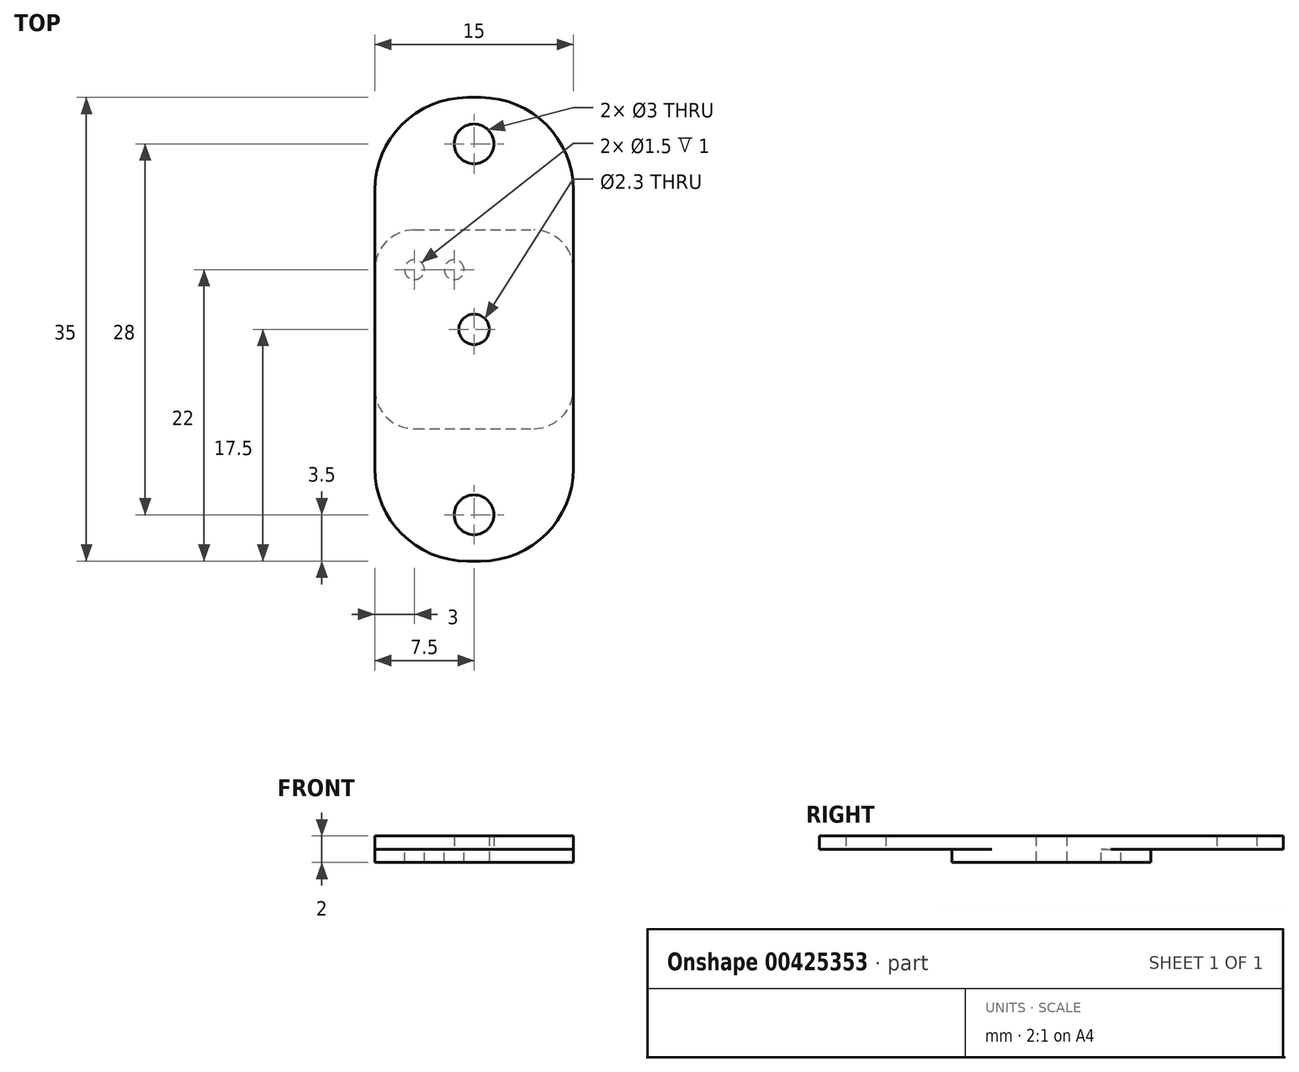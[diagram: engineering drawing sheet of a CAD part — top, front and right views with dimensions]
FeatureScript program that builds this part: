
annotation { "Feature Type Name" : "Feature", "Feature Type Description" : "" }
export const myFeature = defineFeature(function(context is Context, id is Id, definition is map)
    precondition{}
    {
        {
            var Q0;
            Q0=qCreatedBy(makeId("Top.planeOp"),FACE);
            var sketch = newSketch(context, id + "F0", { "sketchPlane" : qUnion([Q0])});
            skCircle(sketch, "E0", {"center": v(0, 0) * mm, "radius": 1.15 * mm});
            skCircle(sketch, "E1", {"center": v(0, 0) * mm, "radius": 2.5 * mm});
            skSolve(sketch);
        }
        {
            var Q0;
            Q0=makeQuery(id+"F0.imprint","IMPRINT",FACE,{"disambiguationData":[TD([[makeQuery(id+"F0.imprint","IMPRINT",EDGE,{"derivedFrom":sQuery(id+"F0.wireOp",EDGE,"E0")}),-1.0]])]});
            extrude(context, id + "F1", {"entities" : qUnion([Q0]), "depth" : 1 * mm});
        }
        {
            var Q0;
            Q0=makeQuery(id+"F1.opExtrude","CAP_FACE",FACE,{"disambiguationData":[OSD([sQuery(id+"F0.wireOp",EDGE,"E0"),sQuery(id+"F0.wireOp",EDGE,"E1")])],"isStart":true});
            var sketch = newSketch(context, id + "F2", { "sketchPlane" : qUnion([Q0])});
            skCircle(sketch, "E2", {"center": v(0, 0) * mm, "radius": 1.15 * mm});
            skCircle(sketch, "E3", {"center": v(0, 0) * mm, "radius": 5 * mm});
            skLineSegment(sketch, "E4.bottom", {"start": v(-7.5, -7.5) * mm, "end": v(7.5, -7.5) * mm});
            skLineSegment(sketch, "E4.top", {"start": v(-7.5, 7.5) * mm, "end": v(7.5, 7.5) * mm});
            skLineSegment(sketch, "E4.left", {"start": v(-7.5, -7.5) * mm, "end": v(-7.5, 7.5) * mm});
            skLineSegment(sketch, "E4.right", {"start": v(7.5, -7.5) * mm, "end": v(7.5, 7.5) * mm});
            skSolve(sketch);
        }
        {
            var Q0;
            Q0=makeQuery(id+"F2.imprint","IMPRINT",FACE,{"disambiguationData":[TD([[makeQuery(id+"F2.imprint","IMPRINT",EDGE,{"derivedFrom":sQuery(id+"F2.wireOp",EDGE,"E3")}),-1.0]])]});
            var Q1;
            Q1=makeQuery(id+"F2.imprint","IMPRINT",FACE,{"disambiguationData":[TD([[makeQuery(id+"F2.imprint","IMPRINT",EDGE,{"derivedFrom":sQuery(id+"F2.wireOp",EDGE,"E3")}),1.0]])]});
            var Q2;
            Q2=makeQuery(id+"F2.imprint","IMPRINT",FACE,{"disambiguationData":[TD([[makeQuery(id+"F2.imprint","IMPRINT",EDGE,{"derivedFrom":sQuery(id+"F2.wireOp",EDGE,"E2")}),1.0]])]});
            extrude(context, id + "F3", {"entities" : qUnion([Q0, Q1, Q2]), "operationType" : NewBodyOperationType.ADD, "depth" : 1 * mm});
        }
        {
            var Q0;
            Q0=makeQuery(id+"F3.opExtrude","SWEPT_EDGE",EDGE,{"disambiguationData":[OSD([sQuery(id+"F2.wireOp",EDGE,"E4.bottom"),sQuery(id+"F2.wireOp",EDGE,"E4.left")])]});
            var Q1;
            Q1=makeQuery(id+"F3.opExtrude","SWEPT_EDGE",EDGE,{"disambiguationData":[OSD([sQuery(id+"F2.wireOp",EDGE,"E4.bottom"),sQuery(id+"F2.wireOp",EDGE,"E4.right")])]});
            var Q2;
            Q2=makeQuery(id+"F3.opExtrude","SWEPT_EDGE",EDGE,{"disambiguationData":[OSD([sQuery(id+"F2.wireOp",EDGE,"E4.top"),sQuery(id+"F2.wireOp",EDGE,"E4.left")])]});
            var Q3;
            Q3=makeQuery(id+"F3.opExtrude","SWEPT_EDGE",EDGE,{"disambiguationData":[OSD([sQuery(id+"F2.wireOp",EDGE,"E4.top"),sQuery(id+"F2.wireOp",EDGE,"E4.right")])]});
            fillet(context, id + "F4", {"entities" : qUnion([Q0, Q1, Q2, Q3]), "radius" : 3 * mm, "tangentPropagation" : true, "allowEdgeOverflow" : false});
        }
        {
            var Q0;
            Q0=makeQuery(id+"F3.opExtrude","CAP_FACE",FACE,{"disambiguationData":[OSD([sQuery(id+"F2.wireOp",EDGE,"E2"),sQuery(id+"F2.wireOp",EDGE,"E4.bottom"),sQuery(id+"F2.wireOp",EDGE,"E4.top"),sQuery(id+"F2.wireOp",EDGE,"E4.left"),sQuery(id+"F2.wireOp",EDGE,"E4.right")])],"isStart":true});
            var sketch = newSketch(context, id + "F5", { "sketchPlane" : qUnion([Q0])});
            skCircle(sketch, "E5", {"center": v(-4.5, 4.5) * mm, "radius": 0.75 * mm});
            skCircle(sketch, "E6", {"center": v(-1.5, 4.5) * mm, "radius": 0.75 * mm});
            skSolve(sketch);
        }
        {
            var Q0;
            Q0=makeQuery(id+"F5.imprint","IMPRINT",FACE,{"disambiguationData":[TD([[makeQuery(id+"F5.imprint","IMPRINT",EDGE,{"derivedFrom":sQuery(id+"F5.wireOp",EDGE,"E5")}),-1.0]])]});
            var sketch = newSketch(context, id + "F6", { "sketchPlane" : qUnion([Q0])});
            skLineSegment(sketch, "E7.bottom", {"start": v(7.5, -17.5) * mm, "end": v(-7.5, -17.5) * mm});
            skLineSegment(sketch, "E7.top", {"start": v(7.5, 17.5) * mm, "end": v(-7.5, 17.5) * mm});
            skLineSegment(sketch, "E7.left", {"start": v(7.5, -17.5) * mm, "end": v(7.5, 17.5) * mm});
            skLineSegment(sketch, "E7.right", {"start": v(-7.5, -17.5) * mm, "end": v(-7.5, 17.5) * mm});
            skPoint(sketch, "E7.middle", {"position": v(0, 0) * mm});
            skCircle(sketch, "E8", {"center": v(0, 14) * mm, "radius": 1.5 * mm});
            skCircle(sketch, "E9", {"center": v(0, -14) * mm, "radius": 1.5 * mm});
            skCircle(sketch, "E10", {"center": v(0, 0) * mm, "radius": 1.15 * mm});
            skSolve(sketch);
        }
        {
            var Q0;
            Q0=qSketchRegion(id+"F6",true);
            extrude(context, id + "F7", {"entities" : qUnion([Q0]), "operationType" : NewBodyOperationType.ADD, "depth" : 1 * mm});
        }
        {
            var Q0;
            Q0=makeQuery(id+"F7.opExtrude","SWEPT_EDGE",EDGE,{"disambiguationData":[OSD([sQuery(id+"F6.wireOp",EDGE,"E7.top"),sQuery(id+"F6.wireOp",EDGE,"E7.right")])]});
            var Q1;
            Q1=makeQuery(id+"F7.opExtrude","SWEPT_EDGE",EDGE,{"disambiguationData":[OSD([sQuery(id+"F6.wireOp",EDGE,"E7.top"),sQuery(id+"F6.wireOp",EDGE,"E7.left")])]});
            var Q2;
            Q2=makeQuery(id+"F7.opExtrude","SWEPT_EDGE",EDGE,{"disambiguationData":[OSD([sQuery(id+"F6.wireOp",EDGE,"E7.bottom"),sQuery(id+"F6.wireOp",EDGE,"E7.left")])]});
            var Q3;
            Q3=makeQuery(id+"F7.opExtrude","SWEPT_EDGE",EDGE,{"disambiguationData":[OSD([sQuery(id+"F6.wireOp",EDGE,"E7.bottom"),sQuery(id+"F6.wireOp",EDGE,"E7.right")])]});
            fillet(context, id + "F8", {"entities" : qUnion([Q0, Q1, Q2, Q3]), "radius" : 7 * mm, "tangentPropagation" : true, "allowEdgeOverflow" : false});
        }
        {
            var Q0;
            Q0=qSketchRegion(id+"F5",true);
            extrude(context, id + "F9", {"entities" : qUnion([Q0]), "operationType" : NewBodyOperationType.REMOVE, "oppositeDirection" : true, "depth" : 25 * mm});
        }
    });
